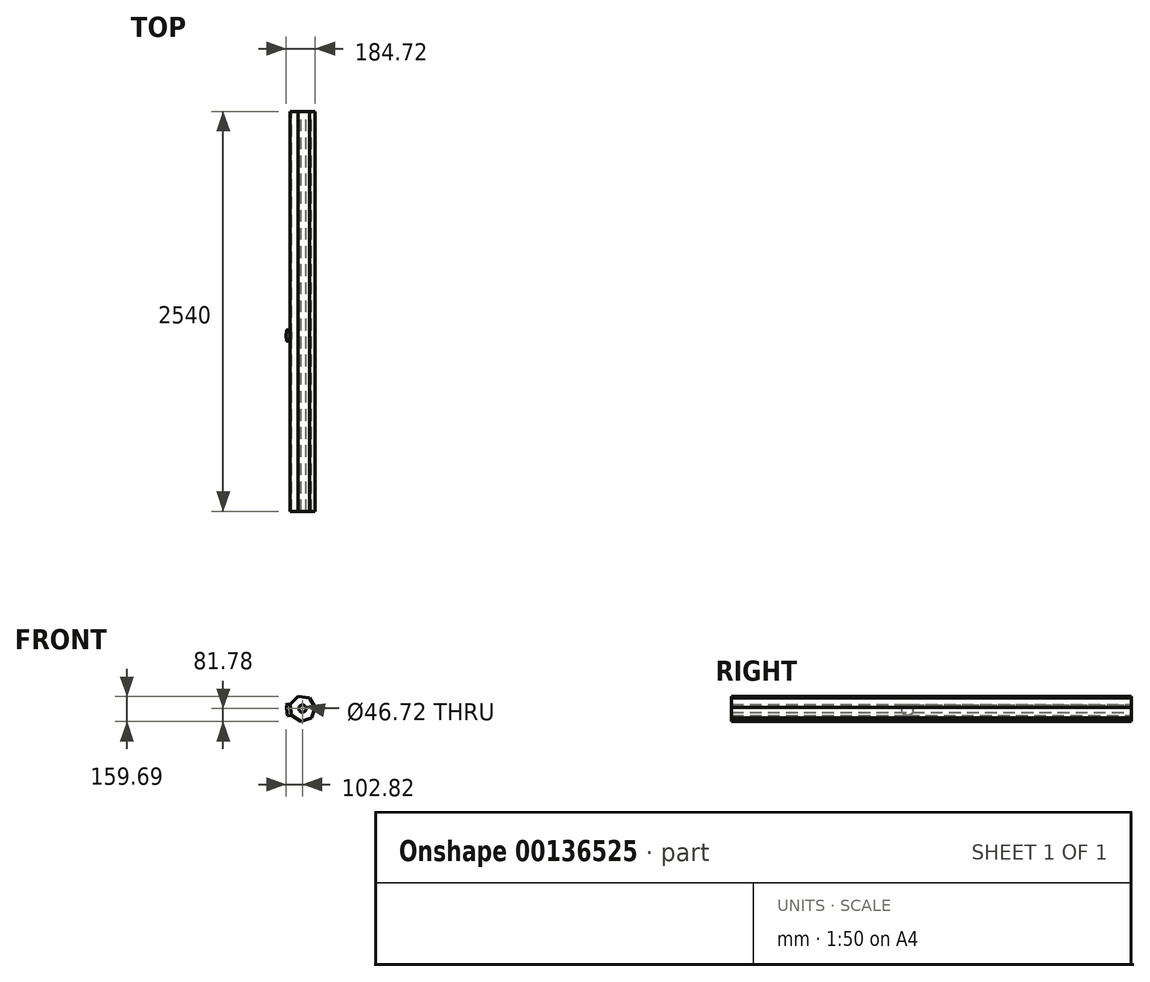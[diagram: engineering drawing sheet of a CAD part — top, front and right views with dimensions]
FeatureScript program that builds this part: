
annotation { "Feature Type Name" : "Feature", "Feature Type Description" : "" }
export const myFeature = defineFeature(function(context is Context, id is Id, definition is map)
    precondition{}
    {
        {
            var Q0;
            Q0=qCreatedBy(makeId("Front.planeOp"),FACE);
            var sketch = newSketch(context, id + "F0", { "sketchPlane" : qUnion([Q0])});
            skCircle(sketch, "E0", {"center": v(0, 0) * mm, "radius": 23.36 * mm});
            skSolve(sketch);
        }
        {
            var Q0;
            Q0=makeQuery(id+"F0.imprint","IMPRINT",FACE,{"disambiguationData":[TD([[makeQuery(id+"F0.imprint","IMPRINT",EDGE,{"derivedFrom":sQuery(id+"F0.wireOp",EDGE,"E0")}),1.0]])]});
            var sketch = newSketch(context, id + "F1", { "sketchPlane" : qUnion([Q0])});
            skCircle(sketch, "E1.cCircle", {"center": v(0, 0) * mm, "radius": 74.2 * mm, "construction": true});
            skLineSegment(sketch, "E1.0", {"start": v(44.26, 69.45) * mm, "end": v(81.9, 8.7) * mm});
            skLineSegment(sketch, "E1.1", {"start": v(81.9, 8.7) * mm, "end": v(57.86, -58.6) * mm});
            skLineSegment(sketch, "E1.2", {"start": v(57.86, -58.6) * mm, "end": v(-9.74, -81.78) * mm});
            skLineSegment(sketch, "E1.3", {"start": v(-9.74, -81.78) * mm, "end": v(-70.01, -43.37) * mm});
            skLineSegment(sketch, "E1.4", {"start": v(-70.01, -43.37) * mm, "end": v(-77.56, 27.7) * mm});
            skLineSegment(sketch, "E1.5", {"start": v(-77.56, 27.7) * mm, "end": v(-26.7, 77.91) * mm});
            skLineSegment(sketch, "E1.6", {"start": v(-26.7, 77.91) * mm, "end": v(44.26, 69.45) * mm});
            skPoint(sketch, "E1.0.midPoint", {"position": v(63.08, 39.08) * mm});
            skSolve(sketch);
        }
        {
            var Q0;
            Q0=makeQuery(id+"F1.imprint","IMPRINT",FACE,{"disambiguationData":[TD([[makeQuery(id+"F1.imprint","IMPRINT",EDGE,{"derivedFrom":sQuery(id+"F1.wireOp",EDGE,"E1.0")}),-1.0]])]});
            extrude(context, id + "F2", {"entities" : qUnion([Q0]), "endBound" : BoundingType.SYMMETRIC, "depth" : 2540 * mm});
        }
        {
            var Q0;
            Q0=makeQuery(id+"F2.opExtrude","SWEPT_FACE",FACE,{"disambiguationData":[OSD([sQuery(id+"F1.wireOp",EDGE,"E1.4")])]});
            var sketch = newSketch(context, id + "F3", { "sketchPlane" : qUnion([Q0])});
            skCircle(sketch, "E2", {"center": v(153.22, 0) * mm, "radius": 35.73 * mm});
            skSolve(sketch);
        }
        {
            var Q0;
            Q0 = qSketchRegion(id + "F3", true);
            extrude(context, id + "F4", {"entities" : qUnion([Q0]), "operationType" : NewBodyOperationType.ADD, "depth" : 25.4 * mm});
        }
    });
